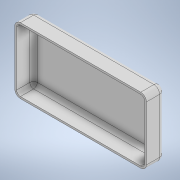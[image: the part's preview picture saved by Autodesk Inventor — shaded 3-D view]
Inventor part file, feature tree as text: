
AUTODESK INVENTOR PART (.ipt)
format: ipt  version: 2021 (Build 250183000, 183)  size: 137,216 bytes
history: native  units: mm
features: fillet x2, other x1, extrude x1, shell x1, sketch x1
ambient origin geometry x8: Origin, YZ Plane, XZ Plane, XY Plane, X Axis, Y Axis, Z Axis, Center Point
bodies: Body1 (feature_tree)
feature tree (6):
  other  "Sólido1"
  extrude  "Extrusão1"  Depth=35.0mm
  fillet  "Arredondamento1"  Radius=10.0mm
  fillet  "Arredondamento2"  Radius=3.0mm
  shell  "Casca1"  Thickness=3.0mm
  sketch  "Esboço1"  dims[d0=70.0mm d1=35.0mm d2=10.0mm d3=0.0mm d4=3.0mm d5=3.0mm d6=1.0mm]
